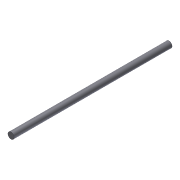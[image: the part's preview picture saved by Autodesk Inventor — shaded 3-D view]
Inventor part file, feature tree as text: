
AUTODESK INVENTOR PART (.ipt)
format: ipt  version: 2012 (Build 160160000, 160)  size: 64,512 bytes
history: native  units: in
note: dims shown in document units (in); Inventor stores cm internally (conversion verified against a paired STEP export)
features: extrude x1, sketch x1
ambient origin geometry x8: Origin, YZ Plane, XZ Plane, XY Plane, X Axis, Y Axis, Z Axis, Center Point
bodies: Solid1 (feature_tree)
feature tree (2):
  extrude  "Extrusion1"  Depth=8.0in TaperAngle=0.0deg
  sketch  "Sketch1"  dims[d0=0.3125in d1=8.0in d2=0.0in]
